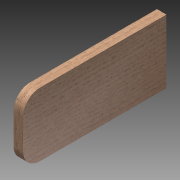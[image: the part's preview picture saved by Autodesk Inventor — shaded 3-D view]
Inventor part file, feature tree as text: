
AUTODESK INVENTOR PART (.ipt)
format: ipt  version: 2013 (Build 170138000, 138)  size: 100,352 bytes
history: native  units: in
note: dims shown in document units (in); Inventor stores cm internally (conversion verified against a paired STEP export)
features: extrude x1, fillet x1, sketch x1
ambient origin geometry x8: Origin, YZ Plane, XZ Plane, XY Plane, X Axis, Y Axis, Z Axis, Center Point
bodies: Solid1 (feature_tree)
feature tree (3):
  extrude  "Extrusion1"  Depth=0.75in
  fillet  "Fillet1"  Radius=11.25in
  sketch  "Sketch1"  dims[d0=5.0in d1=0.75in d2=11.25in d3=0.0in d4=1.3125in]
